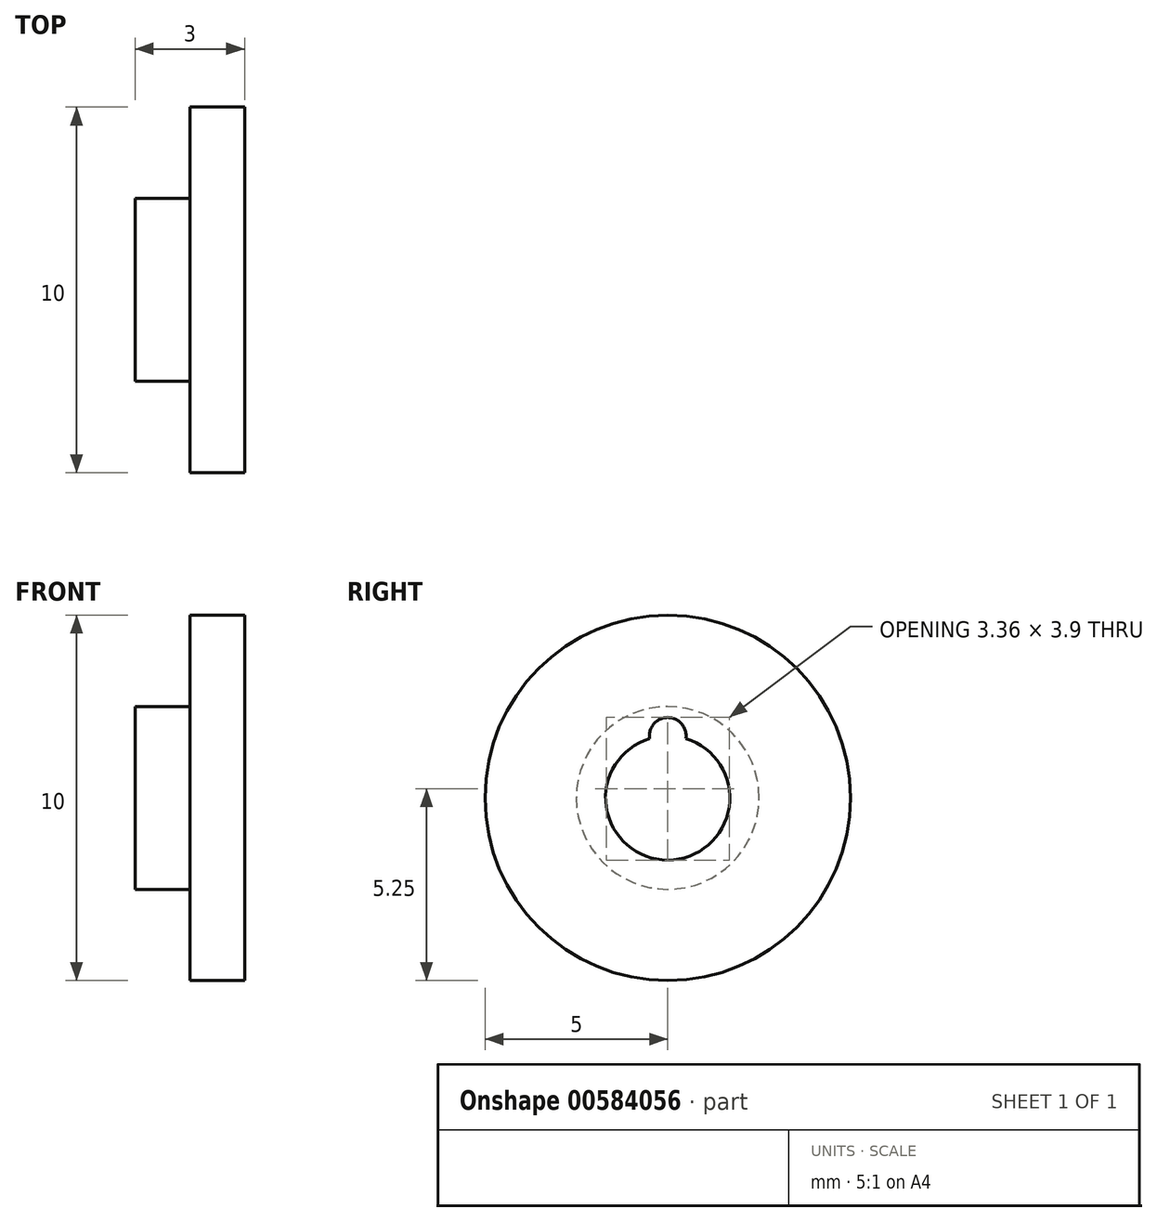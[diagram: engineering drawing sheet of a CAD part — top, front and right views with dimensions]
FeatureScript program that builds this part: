
annotation { "Feature Type Name" : "Feature", "Feature Type Description" : "" }
export const myFeature = defineFeature(function(context is Context, id is Id, definition is map)
    precondition{}
    {
        {
            var Q0;
            Q0=qCreatedBy(makeId("Right.planeOp"),FACE);
            var sketch = newSketch(context, id + "F0", { "sketchPlane" : qUnion([Q0])});
            skCircle(sketch, "E0", {"center": v(0, 0) * mm, "radius": 5 * mm});
            skCircle(sketch, "E1", {"center": v(0, 0) * mm, "radius": 1.7 * mm});
            skSolve(sketch);
        }
        {
            var Q0;
            Q0=makeQuery(id+"F0.imprint","IMPRINT",FACE,{"disambiguationData":[TD([[makeQuery(id+"F0.imprint","IMPRINT",EDGE,{"derivedFrom":sQuery(id+"F0.wireOp",EDGE,"E0")}),1.0]])]});
            extrude(context, id + "F1", {"entities" : qUnion([Q0]), "depth" : 1.5 * mm, "offsetDistance" : 25 * mm});
        }
        {
            var Q0;
            Q0=makeQuery(id+"F1.opExtrude","CAP_FACE",FACE,{"disambiguationData":[OSD([sQuery(id+"F0.wireOp",EDGE,"E0"),sQuery(id+"F0.wireOp",EDGE,"E1")])],"isStart":true});
            var sketch = newSketch(context, id + "F2", { "sketchPlane" : qUnion([Q0])});
            skCircle(sketch, "E2", {"center": v(0, 0) * mm, "radius": 1.7 * mm});
            skCircle(sketch, "E3", {"center": v(0, 0) * mm, "radius": 2.5 * mm});
            skSolve(sketch);
        }
        {
            var Q0;
            Q0 = qSketchRegion(id + "F2", true);
            extrude(context, id + "F3", {"entities" : qUnion([Q0]), "operationType" : NewBodyOperationType.ADD, "depth" : 1.5 * mm, "offsetDistance" : 25 * mm});
        }
        {
            var Q0;
            Q0=makeQuery(id+"F3.opExtrude","CAP_FACE",FACE,{"disambiguationData":[OSD([sQuery(id+"F2.wireOp",EDGE,"E2"),sQuery(id+"F2.wireOp",EDGE,"E3")])],"isStart":false});
            var sketch = newSketch(context, id + "F4", { "sketchPlane" : qUnion([Q0])});
            skLineSegment(sketch, "E4", {"start": v(0, 2.5) * mm, "end": v(0, 1.7) * mm});
            skSolve(sketch);
        }
        {
            var Q0;
            Q0=sQuery(id+"F4.wireOp",VERTEX,"E4.end");
            var Q1;
            Q1=makeQuery(id+"F1.opExtrude","SWEPT_BODY",BODY,{"disambiguationData":[OSD([sQuery(id+"F0.wireOp",EDGE,"E0"),sQuery(id+"F0.wireOp",EDGE,"E1")])]});
            hole(context, id + "F5", {"style" : HoleStyle.SIMPLE, "endStyle" : HoleEndStyle.THROUGH, "holeDiameter" : 1 * mm, "majorDiameter" : 5 * mm, "isTappedThrough" : true, "tappedDepth" : 12 * mm, "tapClearance" : 3, "locations" : qUnion([Q0]), "scope" : qUnion([Q1])});
        }
    });
